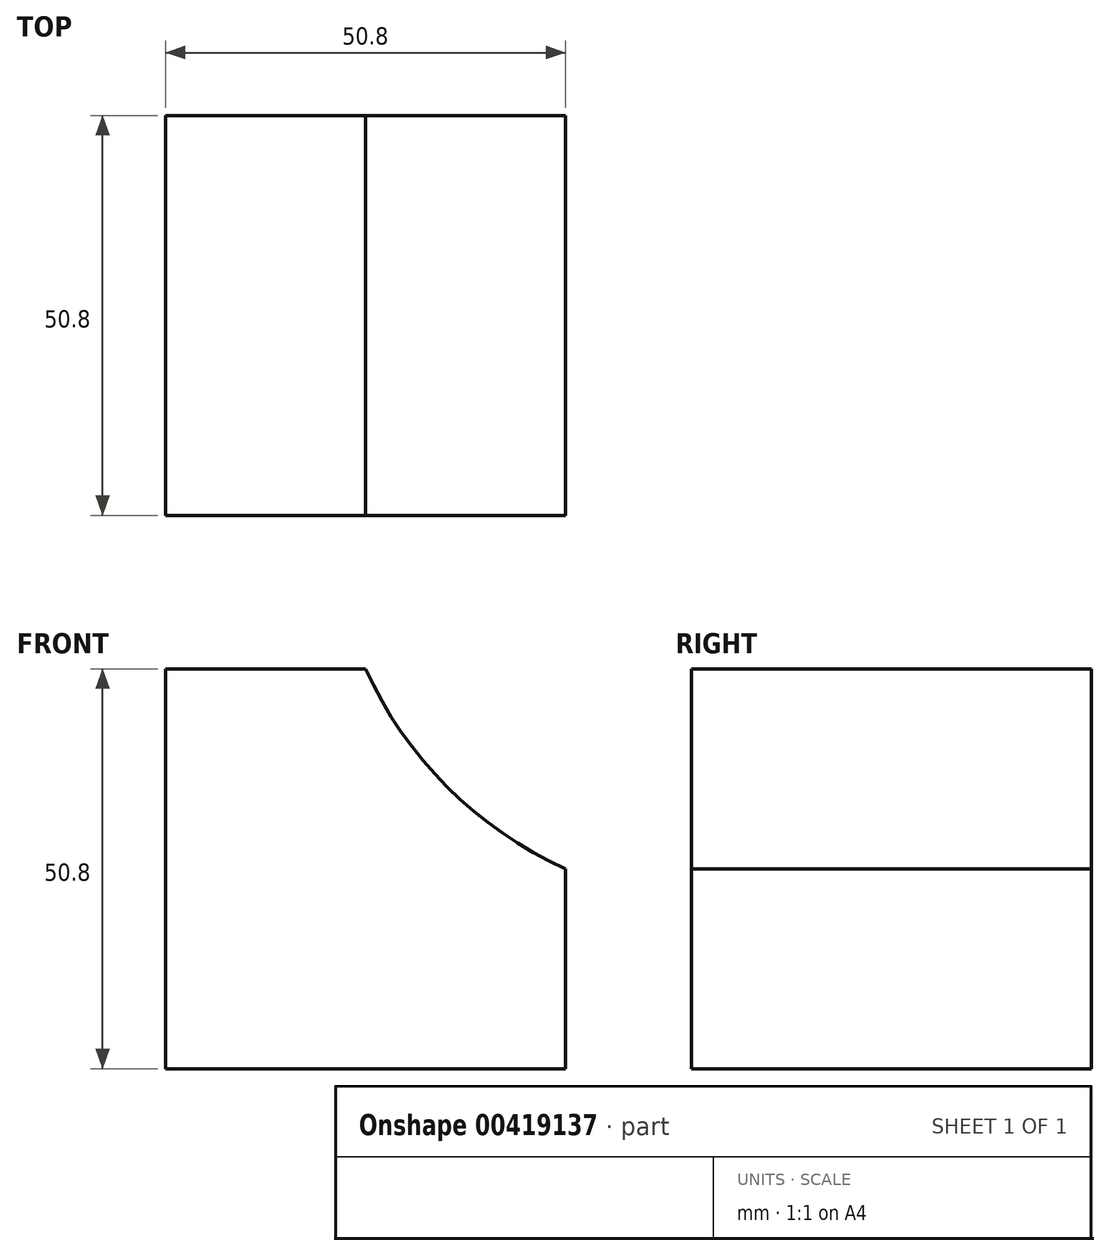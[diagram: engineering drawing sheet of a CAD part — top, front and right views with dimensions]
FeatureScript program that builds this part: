
annotation { "Feature Type Name" : "Feature", "Feature Type Description" : "" }
export const myFeature = defineFeature(function(context is Context, id is Id, definition is map)
    precondition{}
    {
        {
            var Q0;
            Q0=qCreatedBy(makeId("Front.planeOp"),FACE);
            var sketch = newSketch(context, id + "F0", { "sketchPlane" : qUnion([Q0])});
            skLineSegment(sketch, "E0", {"start": v(0, 0) * mm, "end": v(-50.8, 0) * mm});
            skLineSegment(sketch, "E1", {"start": v(-50.8, 0) * mm, "end": v(-50.8, 50.8) * mm});
            skLineSegment(sketch, "E2", {"start": v(-50.8, 50.8) * mm, "end": v(-25.4, 50.8) * mm});
            skLineSegment(sketch, "E3", {"start": v(0, 0) * mm, "end": v(0, 25.4) * mm});
            skArc(sketch, "E4", {"start": v(-25.4, 50.8) * mm, "mid": v(-15.02, 35.78) * mm, "end": v(0, 25.4) * mm});
            skSolve(sketch);
        }
        {
            var Q0;
            Q0 = qSketchRegion(id + "F0", true);
            extrude(context, id + "F1", {"entities" : qUnion([Q0]), "depth" : 50.8 * mm});
        }
    });
